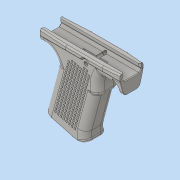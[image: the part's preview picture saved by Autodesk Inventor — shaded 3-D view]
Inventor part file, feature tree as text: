
AUTODESK INVENTOR PART (.ipt)
format: ipt  version: 2016 (Build 200138000, 138)  size: 3,090,944 bytes
history: native  units: in
note: dims shown in document units (in); Inventor stores cm internally (conversion verified against a paired STEP export)
features: fillet x21, sketch x20, extrude x19, chamfer x10, projected_geometry x2, revolve x1
ambient origin geometry x8: Origin, YZ Plane, XZ Plane, XY Plane, X Axis, Y Axis, Z Axis, Center Point
bodies: Solid1 (feature_tree)
feature tree (73):
  extrude  "Extrusion1"  Depth=3.0in
  extrude  "Extrusion2"  Depth=0.3125in
  extrude  "Extrusion3"  Depth=0.22in
  extrude  "Extrusion4"  Depth=0.1in
  fillet  "Fillet1"  Radius=0.1in
  fillet  "Fillet2"  Radius=0.1in
  fillet  "Fillet3"  Radius=0.1in
  extrude  "Extrusion5"  Depth=0.1in
  revolve  "Revolution1"  [1 undecoded]
  extrude  "Extrusion6"  Depth=0.3125in
  extrude  "Extrusion7"  Depth=3.0in TaperAngle=0.0deg
  extrude  "Extrusion8"  TaperAngle=105.0deg  [1 undecoded]
  fillet  "Fillet4"  Radius=0.5in
  extrude  "Extrusion9"  Depth=0.875in
  fillet  "Fillet5"  Radius=0.75in
  fillet  "Fillet6"  [1 undecoded]
  fillet  "Fillet7"  Radius=3.0in
  extrude  "Extrusion10"  Depth=0.125in
  fillet  "Fillet8"  Radius=0.125in
  fillet  "Fillet9"  Radius=3.0in
  extrude  "Extrusion11"  Depth=0.5in
  fillet  "Fillet10"  [1 undecoded]
  fillet  "Fillet11"  Radius=0.125in
  extrude  "Extrusion12"  Depth=0.25in TaperAngle=0.0deg
  fillet  "Fillet12"  Radius=0.25in
  fillet  "Fillet13"  Radius=0.375in
  fillet  "Fillet14"  Radius=0.1875in
  extrude  "Extrusion13"  Depth=0.1875in
  extrude  "Extrusion14"  Depth=0.5in
  extrude  "Extrusion15"  TaperAngle=165.0deg  [1 undecoded]
  chamfer  "Chamfer1"  Distance=1.0in
  chamfer  "Chamfer2"  Distance=1.0in
  chamfer  "Chamfer3"  Distance=0.75in
  chamfer  "Chamfer4"  Distance=0.5in
  extrude  "Extrusion16"  Depth=0.5in TaperAngle=0.0deg
  extrude  "Extrusion17"  Depth=0.25in
  chamfer  "Chamfer5"  Distance=0.0625in
  chamfer  "Chamfer6"  Distance=0.25in
  chamfer  "Chamfer7"  Distance=0.5in
  chamfer  "Chamfer8"  Distance=0.3125in
  chamfer  "Chamfer9"  Distance=0.125in
  chamfer  "Chamfer10"  Distance=0.0625in
  fillet  "Fillet15"  Radius=0.0625in
  fillet  "Fillet16"  Radius=0.0625in
  fillet  "Fillet17"  Radius=0.0625in
  fillet  "Fillet18"  Radius=0.0625in
  fillet  "Fillet19"  Radius=0.0625in
  fillet  "Fillet20"  Radius=0.0625in
  fillet  "Fillet21"  Radius=0.0625in
  extrude  "Extrusion18"  Depth=0.0625in
  extrude  "Extrusion19"  Depth=0.0625in
  sketch  "Sketch1"  dims[d0=1.0in d1=3.0in]
  sketch  "Sketch2"  dims[d2=3.0in d3=0.0in d4=0.3125in]
  sketch  "Sketch3"  dims[d6=0.835in d7=0.22in]
  sketch  "Sketch4"  dims[d8=0.1in d9=0.1in d10=0.1in d11=0.1in d12=0.1in]
  sketch  "Sketch5"  dims[d13=0.1in d14=0.1in]
  sketch  "Sketch6"  dims[d15=0.1in d16=0.6875in]
  sketch  "Sketch7"  dims[d17=3.0in d18=0.0in d19=0.3125in]
  sketch  "Sketch8"  dims[d20=0.136in d21=3.0in d22=0.0in]
  sketch  "Sketch9"  dims[d23=0.5in d25=105.0deg d26=0.5in]
  sketch  "Sketch10"  dims[d28=1.0in d29=0.875in d30=0.75in d31=105.0deg d32=3.0in d33=0.0in]
  sketch  "Sketch11"  dims[d34=0.3125in d35=0.125in d36=0.125in d37=3.0in d38=0.0in]
  sketch  "Sketch12"  dims[d39=0.5in d40=0.5in d41=30.0deg d42=0.125in d43=0.0in]
  sketch  "Sketch13"  dims[d44=1.0in d45=0.0in d46=1.0in d47=0.0in d48=0.25in d54=0.375in d55=0.1875in d56=0.0in]
  sketch  "Sketch14"  dims[d57=0.1875in d58=0.1875in]
  sketch  "Sketch15"  dims[d59=0.0625in d60=0.5in]
  sketch  "Sketch16"  dims[d61=1.75in d62=165.0deg d63=1.0in d64=0.0in]
  projected_geometry  "Projected Loop1"
  sketch  "Sketch17"  dims[d65=0.375in]
  sketch  "Sketch18"  dims[d66=0.5in d67=1.0in d68=0.0in]
  projected_geometry  "Projected Loop2"
  sketch  "Sketch19"  dims[d69=1.0in]
  sketch  "Sketch20"  dims[d70=0.0625in d71=0.75in d72=0.5in d73=2.75in d74=0.0in d75=0.25in d76=0.0625in d77=0.25in d78=0.5in d79=0.0in d80=0.3125in d81=0.125in d82=0.0625in d83=0.0625in d84=0.0625in d85=0.0625in d86=0.0625in d87=0.0625in d88=0.0625in d89=0.0625in d90=0.0625in d91=0.0625in d92=0.0625in d93=0.0625in d94=0.0625in d95=0.0625in d96=0.0625in d97=0.0625in d98=0.0625in d99=0.0625in d100=0.0625in d101=0.0625in d102=0.0625in d103=0.0625in d104=0.0625in d105=0.0625in d106=0.0625in d107=0.0625in d108=0.0625in d109=0.0625in d110=0.0625in d111=0.0625in d112=0.0625in d113=0.0625in d114=0.0625in d115=0.0625in d116=0.0625in d117=0.0625in d118=0.0625in d119=0.0625in d120=0.0625in d121=0.0625in d122=0.0625in d123=0.0625in d124=0.0625in d125=0.0625in d126=0.0625in d127=0.0625in d128=0.0625in d129=0.0625in d130=0.0625in d131=0.0625in d132=0.0625in d133=0.0625in d134=0.0625in d135=0.0625in d136=0.0625in d137=0.0625in d138=0.0625in d139=0.0625in d140=0.0625in d141=0.0625in d142=0.0625in d143=0.0625in d144=0.0625in d145=0.0625in d146=0.0625in d147=0.0625in d148=0.0625in d149=0.0625in d150=0.0625in d151=0.0625in d152=0.0625in d153=0.0625in d154=0.0625in d155=0.0625in d156=0.0625in d157=0.0625in d158=0.0625in d159=0.0625in d160=0.0625in d161=0.0625in d162=0.0625in d163=0.0625in d164=0.0625in d165=0.0625in d166=0.0625in d167=0.0625in d168=0.0625in d169=0.0625in d170=0.0625in d171=0.0625in d172=0.0625in d173=0.0625in d174=0.0625in d175=0.0625in d176=0.0625in d177=0.0625in d178=0.0625in d179=0.0625in d180=0.0625in d181=0.0625in d182=0.0625in d183=0.0625in d184=0.0625in d185=0.0625in d186=0.0625in d187=0.0625in d188=0.0625in d189=0.0625in d190=0.0625in d191=0.0625in d192=0.0625in d193=0.0625in d194=0.0625in d195=0.0625in d196=0.0625in d197=0.0625in d198=0.0625in d199=0.0625in d200=0.0625in d201=0.0625in d202=0.0625in d203=0.0625in d204=0.0625in d205=0.0625in d206=0.0625in d207=0.0625in d208=0.0625in d209=0.0625in d210=0.0625in d211=0.0625in d212=0.0625in d213=0.0625in d214=0.0625in d215=0.0625in d216=0.0625in d217=0.0625in d218=0.0625in d219=0.0625in d220=0.0625in d221=0.0625in d222=0.0625in d223=0.0625in d224=0.0625in d225=0.0625in d226=0.0625in d227=0.0625in d228=0.0625in d229=0.0625in d230=0.0625in d231=0.0625in d232=0.0625in d233=0.0625in d234=0.0625in d236=0.0625in d237=0.0625in d238=0.0625in d239=0.0625in d240=0.0625in d241=0.0625in d242=0.0625in d248=0.0625in d249=0.0625in d251=0.0156in d252=0.0in d253=0.0156in d254=0.0in d255=0.0625in d256=0.125in d257=45.0deg d258=0.0312in d259=0.125in d260=45.0deg d261=0.0312in d262=0.125in d263=45.0deg d264=0.0625in d265=0.125in d266=45.0deg d267=0.033in d268=0.33in d269=0.0625in d270=0.0in d271=0.0625in d272=0.0in d273=0.0625in d274=0.125in d275=45.0deg d276=0.0625in d277=0.125in d278=45.0deg d279=0.0625in d280=0.125in d281=0.5841in d282=0.0625in d283=0.125in d284=0.5841in d285=0.0625in d286=0.125in d287=0.5978in d288=0.0625in d289=0.125in d290=0.5978in d291=0.0625in d292=0.0625in d293=0.0312in d294=0.0625in d295=0.0312in d296=0.0156in d297=0.0156in d298=0.166in d299=0.8in d300=0.0in d301=1.375in d302=0.0in d303=1.0in d304=0.0625in d305=0.0625in d306=0.5in d307=0.0in]
note: 5 required parameter values undecoded (feature->parameter linkage not recoverable at this tier; creation-order binding heuristic only, values carry confidence <= 0.55)